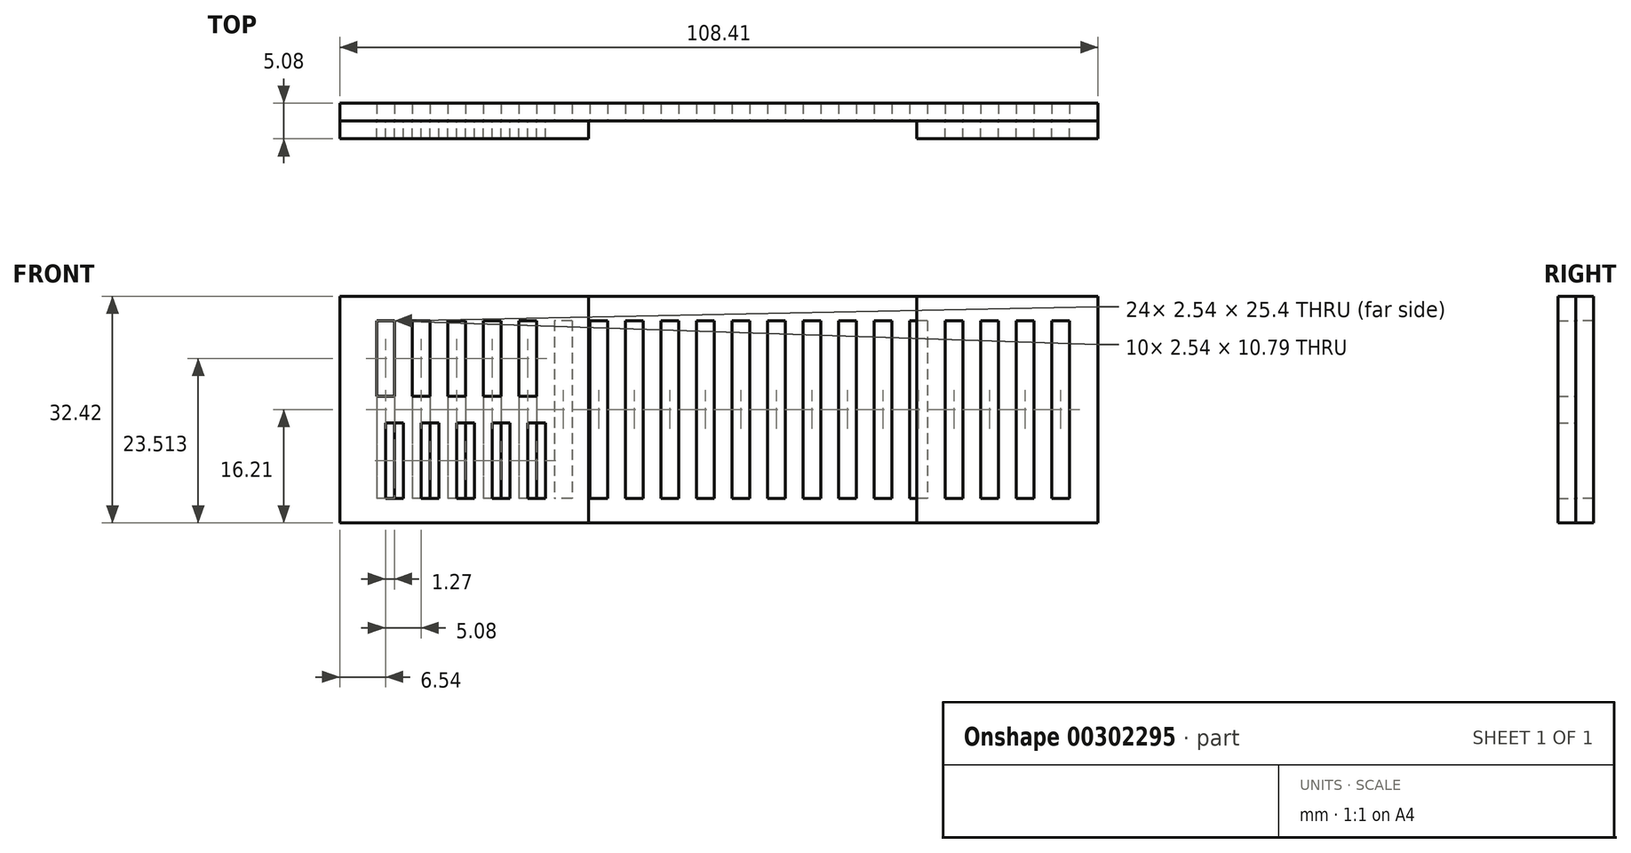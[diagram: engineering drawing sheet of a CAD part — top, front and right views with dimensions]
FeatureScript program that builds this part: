
annotation { "Feature Type Name" : "Feature", "Feature Type Description" : "" }
export const myFeature = defineFeature(function(context is Context, id is Id, definition is map)
    precondition{}
    {
        {
            var Q0;
            Q0=qCreatedBy(makeId("Front.planeOp"),FACE);
            var sketch = newSketch(context, id + "F0", { "sketchPlane" : qUnion([Q0])});
            skLineSegment(sketch, "E0.bottom", {"start": v(1.27, 12.7) * mm, "end": v(-1.27, 12.7) * mm});
            skLineSegment(sketch, "E0.top", {"start": v(1.27, -12.7) * mm, "end": v(-1.27, -12.7) * mm});
            skLineSegment(sketch, "E0.left", {"start": v(1.27, 12.7) * mm, "end": v(1.27, -12.7) * mm});
            skLineSegment(sketch, "E0.right", {"start": v(-1.27, 12.7) * mm, "end": v(-1.27, -12.7) * mm});
            skPoint(sketch, "E0.middle", {"position": v(0, 0) * mm});
            skLineSegment(sketch, "E1.1.0.0", {"start": v(6.35, 12.7) * mm, "end": v(6.35, -12.7) * mm});
            skLineSegment(sketch, "E1.1.0.1", {"start": v(3.81, 12.7) * mm, "end": v(3.81, -12.7) * mm});
            skPoint(sketch, "E1.1.0.2", {"position": v(5.08, 0) * mm});
            skLineSegment(sketch, "E1.1.0.3", {"start": v(6.35, 12.7) * mm, "end": v(3.81, 12.7) * mm});
            skLineSegment(sketch, "E1.1.0.4", {"start": v(6.35, -12.7) * mm, "end": v(3.81, -12.7) * mm});
            skLineSegment(sketch, "E1.2.0.0", {"start": v(11.43, 12.7) * mm, "end": v(11.43, -12.7) * mm});
            skLineSegment(sketch, "E1.2.0.1", {"start": v(8.9, 12.7) * mm, "end": v(8.9, -12.7) * mm});
            skPoint(sketch, "E1.2.0.2", {"position": v(10.16, 0) * mm});
            skLineSegment(sketch, "E1.2.0.3", {"start": v(11.43, 12.7) * mm, "end": v(8.9, 12.7) * mm});
            skLineSegment(sketch, "E1.2.0.4", {"start": v(11.43, -12.7) * mm, "end": v(8.9, -12.7) * mm});
            skLineSegment(sketch, "E1.3.0.0", {"start": v(16.51, 12.7) * mm, "end": v(16.51, -12.7) * mm});
            skLineSegment(sketch, "E1.3.0.1", {"start": v(13.97, 12.7) * mm, "end": v(13.97, -12.7) * mm});
            skPoint(sketch, "E1.3.0.2", {"position": v(15.24, 0) * mm});
            skLineSegment(sketch, "E1.3.0.3", {"start": v(16.51, 12.7) * mm, "end": v(13.97, 12.7) * mm});
            skLineSegment(sketch, "E1.3.0.4", {"start": v(16.51, -12.7) * mm, "end": v(13.97, -12.7) * mm});
            skLineSegment(sketch, "E1.4.0.0", {"start": v(21.6, 12.7) * mm, "end": v(21.6, -12.7) * mm});
            skLineSegment(sketch, "E1.4.0.1", {"start": v(19.05, 12.7) * mm, "end": v(19.05, -12.7) * mm});
            skPoint(sketch, "E1.4.0.2", {"position": v(20.32, 0) * mm});
            skLineSegment(sketch, "E1.4.0.3", {"start": v(21.6, 12.7) * mm, "end": v(19.05, 12.7) * mm});
            skLineSegment(sketch, "E1.4.0.4", {"start": v(21.6, -12.7) * mm, "end": v(19.05, -12.7) * mm});
            skLineSegment(sketch, "E1.5.0.0", {"start": v(26.67, 12.7) * mm, "end": v(26.67, -12.7) * mm});
            skLineSegment(sketch, "E1.5.0.1", {"start": v(24.13, 12.7) * mm, "end": v(24.13, -12.7) * mm});
            skPoint(sketch, "E1.5.0.2", {"position": v(25.4, 0) * mm});
            skLineSegment(sketch, "E1.5.0.3", {"start": v(26.67, 12.7) * mm, "end": v(24.13, 12.7) * mm});
            skLineSegment(sketch, "E1.5.0.4", {"start": v(26.67, -12.7) * mm, "end": v(24.13, -12.7) * mm});
            skLineSegment(sketch, "E1.6.0.0", {"start": v(31.75, 12.7) * mm, "end": v(31.75, -12.7) * mm});
            skLineSegment(sketch, "E1.6.0.1", {"start": v(29.21, 12.7) * mm, "end": v(29.21, -12.7) * mm});
            skPoint(sketch, "E1.6.0.2", {"position": v(30.48, 0) * mm});
            skLineSegment(sketch, "E1.6.0.3", {"start": v(31.75, 12.7) * mm, "end": v(29.21, 12.7) * mm});
            skLineSegment(sketch, "E1.6.0.4", {"start": v(31.75, -12.7) * mm, "end": v(29.21, -12.7) * mm});
            skLineSegment(sketch, "E1.7.0.0", {"start": v(36.83, 12.7) * mm, "end": v(36.83, -12.7) * mm});
            skLineSegment(sketch, "E1.7.0.1", {"start": v(34.3, 12.7) * mm, "end": v(34.3, -12.7) * mm});
            skPoint(sketch, "E1.7.0.2", {"position": v(35.56, 0) * mm});
            skLineSegment(sketch, "E1.7.0.3", {"start": v(36.83, 12.7) * mm, "end": v(34.3, 12.7) * mm});
            skLineSegment(sketch, "E1.7.0.4", {"start": v(36.83, -12.7) * mm, "end": v(34.3, -12.7) * mm});
            skLineSegment(sketch, "E1.8.0.0", {"start": v(41.91, 12.7) * mm, "end": v(41.91, -12.7) * mm});
            skLineSegment(sketch, "E1.8.0.1", {"start": v(39.37, 12.7) * mm, "end": v(39.37, -12.7) * mm});
            skPoint(sketch, "E1.8.0.2", {"position": v(40.64, 0) * mm});
            skLineSegment(sketch, "E1.8.0.3", {"start": v(41.91, 12.7) * mm, "end": v(39.37, 12.7) * mm});
            skLineSegment(sketch, "E1.8.0.4", {"start": v(41.91, -12.7) * mm, "end": v(39.37, -12.7) * mm});
            skLineSegment(sketch, "E1.9.0.0", {"start": v(47, 12.7) * mm, "end": v(47, -12.7) * mm});
            skLineSegment(sketch, "E1.9.0.1", {"start": v(44.45, 12.7) * mm, "end": v(44.45, -12.7) * mm});
            skPoint(sketch, "E1.9.0.2", {"position": v(45.72, 0) * mm});
            skLineSegment(sketch, "E1.9.0.3", {"start": v(47, 12.7) * mm, "end": v(44.45, 12.7) * mm});
            skLineSegment(sketch, "E1.9.0.4", {"start": v(47, -12.7) * mm, "end": v(44.45, -12.7) * mm});
            skLineSegment(sketch, "E1.10.0.0", {"start": v(52.07, 12.7) * mm, "end": v(52.07, -12.7) * mm});
            skLineSegment(sketch, "E1.10.0.1", {"start": v(49.53, 12.7) * mm, "end": v(49.53, -12.7) * mm});
            skPoint(sketch, "E1.10.0.2", {"position": v(50.8, 0) * mm});
            skLineSegment(sketch, "E1.10.0.3", {"start": v(52.07, 12.7) * mm, "end": v(49.53, 12.7) * mm});
            skLineSegment(sketch, "E1.10.0.4", {"start": v(52.07, -12.7) * mm, "end": v(49.53, -12.7) * mm});
            skLineSegment(sketch, "E1.11.0.0", {"start": v(57.15, 12.7) * mm, "end": v(57.15, -12.7) * mm});
            skLineSegment(sketch, "E1.11.0.1", {"start": v(54.61, 12.7) * mm, "end": v(54.61, -12.7) * mm});
            skPoint(sketch, "E1.11.0.2", {"position": v(55.88, 0) * mm});
            skLineSegment(sketch, "E1.11.0.3", {"start": v(57.15, 12.7) * mm, "end": v(54.61, 12.7) * mm});
            skLineSegment(sketch, "E1.11.0.4", {"start": v(57.15, -12.7) * mm, "end": v(54.61, -12.7) * mm});
            skLineSegment(sketch, "E1.12.0.0", {"start": v(62.23, 12.7) * mm, "end": v(62.23, -12.7) * mm});
            skLineSegment(sketch, "E1.12.0.1", {"start": v(59.7, 12.7) * mm, "end": v(59.7, -12.7) * mm});
            skPoint(sketch, "E1.12.0.2", {"position": v(60.96, 0) * mm});
            skLineSegment(sketch, "E1.12.0.3", {"start": v(62.23, 12.7) * mm, "end": v(59.7, 12.7) * mm});
            skLineSegment(sketch, "E1.12.0.4", {"start": v(62.23, -12.7) * mm, "end": v(59.7, -12.7) * mm});
            skLineSegment(sketch, "E1.13.0.0", {"start": v(67.31, 12.7) * mm, "end": v(67.31, -12.7) * mm});
            skLineSegment(sketch, "E1.13.0.1", {"start": v(64.77, 12.7) * mm, "end": v(64.77, -12.7) * mm});
            skPoint(sketch, "E1.13.0.2", {"position": v(66.04, 0) * mm});
            skLineSegment(sketch, "E1.13.0.3", {"start": v(67.31, 12.7) * mm, "end": v(64.77, 12.7) * mm});
            skLineSegment(sketch, "E1.13.0.4", {"start": v(67.31, -12.7) * mm, "end": v(64.77, -12.7) * mm});
            skLineSegment(sketch, "E1.14.0.0", {"start": v(72.4, 12.7) * mm, "end": v(72.4, -12.7) * mm});
            skLineSegment(sketch, "E1.14.0.1", {"start": v(69.85, 12.7) * mm, "end": v(69.85, -12.7) * mm});
            skPoint(sketch, "E1.14.0.2", {"position": v(71.12, 0) * mm});
            skLineSegment(sketch, "E1.14.0.3", {"start": v(72.4, 12.7) * mm, "end": v(69.85, 12.7) * mm});
            skLineSegment(sketch, "E1.14.0.4", {"start": v(72.4, -12.7) * mm, "end": v(69.85, -12.7) * mm});
            skLineSegment(sketch, "E1.15.0.0", {"start": v(77.47, 12.7) * mm, "end": v(77.47, -12.7) * mm});
            skLineSegment(sketch, "E1.15.0.1", {"start": v(74.93, 12.7) * mm, "end": v(74.93, -12.7) * mm});
            skPoint(sketch, "E1.15.0.2", {"position": v(76.2, 0) * mm});
            skLineSegment(sketch, "E1.15.0.3", {"start": v(77.47, 12.7) * mm, "end": v(74.93, 12.7) * mm});
            skLineSegment(sketch, "E1.15.0.4", {"start": v(77.47, -12.7) * mm, "end": v(74.93, -12.7) * mm});
            skLineSegment(sketch, "E1.16.0.0", {"start": v(82.55, 12.7) * mm, "end": v(82.55, -12.7) * mm});
            skLineSegment(sketch, "E1.16.0.1", {"start": v(80.01, 12.7) * mm, "end": v(80.01, -12.7) * mm});
            skPoint(sketch, "E1.16.0.2", {"position": v(81.28, 0) * mm});
            skLineSegment(sketch, "E1.16.0.3", {"start": v(82.55, 12.7) * mm, "end": v(80.01, 12.7) * mm});
            skLineSegment(sketch, "E1.16.0.4", {"start": v(82.55, -12.7) * mm, "end": v(80.01, -12.7) * mm});
            skLineSegment(sketch, "E1.17.0.0", {"start": v(87.63, 12.7) * mm, "end": v(87.63, -12.7) * mm});
            skLineSegment(sketch, "E1.17.0.1", {"start": v(85.1, 12.7) * mm, "end": v(85.1, -12.7) * mm});
            skPoint(sketch, "E1.17.0.2", {"position": v(86.36, 0) * mm});
            skLineSegment(sketch, "E1.17.0.3", {"start": v(87.63, 12.7) * mm, "end": v(85.1, 12.7) * mm});
            skLineSegment(sketch, "E1.17.0.4", {"start": v(87.63, -12.7) * mm, "end": v(85.1, -12.7) * mm});
            skLineSegment(sketch, "E1.18.0.0", {"start": v(92.71, 12.7) * mm, "end": v(92.71, -12.7) * mm});
            skLineSegment(sketch, "E1.18.0.1", {"start": v(90.17, 12.7) * mm, "end": v(90.17, -12.7) * mm});
            skPoint(sketch, "E1.18.0.2", {"position": v(91.44, 0) * mm});
            skLineSegment(sketch, "E1.18.0.3", {"start": v(92.71, 12.7) * mm, "end": v(90.17, 12.7) * mm});
            skLineSegment(sketch, "E1.18.0.4", {"start": v(92.71, -12.7) * mm, "end": v(90.17, -12.7) * mm});
            skLineSegment(sketch, "E1.19.0.0", {"start": v(97.8, 12.7) * mm, "end": v(97.8, -12.7) * mm});
            skLineSegment(sketch, "E1.19.0.1", {"start": v(95.25, 12.7) * mm, "end": v(95.25, -12.7) * mm});
            skPoint(sketch, "E1.19.0.2", {"position": v(96.52, 0) * mm});
            skLineSegment(sketch, "E1.19.0.3", {"start": v(97.8, 12.7) * mm, "end": v(95.25, 12.7) * mm});
            skLineSegment(sketch, "E1.19.0.4", {"start": v(97.8, -12.7) * mm, "end": v(95.25, -12.7) * mm});
            skLineSegment(sketch, "E1.direction1", {"start": v(-1.27, -12.7) * mm, "end": v(3.81, -12.7) * mm, "construction": true});
            skLineSegment(sketch, "E2.bottom", {"start": v(-6.54, -16.21) * mm, "end": v(101.87, -16.21) * mm});
            skLineSegment(sketch, "E2.top", {"start": v(-6.54, 16.21) * mm, "end": v(101.87, 16.21) * mm});
            skLineSegment(sketch, "E2.left", {"start": v(-6.54, -16.21) * mm, "end": v(-6.54, 16.21) * mm});
            skLineSegment(sketch, "E2.right", {"start": v(101.87, -16.21) * mm, "end": v(101.87, 16.21) * mm});
            skLineSegment(sketch, "E3", {"start": v(75.95, 16.21) * mm, "end": v(75.95, -16.21) * mm});
            skSolve(sketch);
        }
        {
            var Q0;
            Q0=makeQuery(id+"F0.imprint","IMPRINT",FACE,{"disambiguationData":[TD([[makeQuery(id+"F0.imprint","IMPRINT",EDGE,{"derivedFrom":sQuery(id+"F0.wireOp",EDGE,"E0.bottom")}),-1.0]])]});
            var Q1;
            {var subQ2=sQuery(id+"F0.wireOp",EDGE,"E1.15.0.0");Q1=makeQuery(id+"F0.imprint","IMPRINT",FACE,{"disambiguationData":[TD([[makeQuery(id+"F0.imprint","IMPRINT",EDGE,{"derivedFrom":subQ2}),1.0]])]});}
            extrude(context, id + "F1", {"entities" : qUnion([Q0, Q1]), "oppositeDirection" : true, "depth" : 2.54 * mm});
        }
        {
            var Q0;
            {var subQ2=sQuery(id+"F0.wireOp",EDGE,"E1.15.0.0");Q0=makeQuery(id+"F0.imprint","IMPRINT",FACE,{"disambiguationData":[TD([[makeQuery(id+"F0.imprint","IMPRINT",EDGE,{"derivedFrom":subQ2}),1.0]])]});}
            var Q1;
            {var subQ0=sQuery(id+"F0.wireOp",EDGE,"E1.15.0.0");Q1=makeQuery(id+"F0.imprint","IMPRINT",FACE,{"disambiguationData":[TD([[makeQuery(id+"F0.imprint","IMPRINT",EDGE,{"derivedFrom":subQ0}),-1.0]])]});}
            extrude(context, id + "F2", {"entities" : qUnion([Q0, Q1]), "depth" : 2.54 * mm});
        }
        {
            var Q0;
            Q0=qCreatedBy(makeId("Front.planeOp"),FACE);
            var sketch = newSketch(context, id + "F3", { "sketchPlane" : qUnion([Q0])});
            skLineSegment(sketch, "E4.0", {"start": v(-6.54, -16.21) * mm, "end": v(-6.54, 16.21) * mm});
            skLineSegment(sketch, "E5.bottom", {"start": v(-6.54, -16.21) * mm, "end": v(29.02, -16.21) * mm});
            skLineSegment(sketch, "E5.top", {"start": v(-6.54, 16.21) * mm, "end": v(29.02, 16.21) * mm});
            skLineSegment(sketch, "E5.right", {"start": v(29.02, -16.21) * mm, "end": v(29.02, 16.21) * mm});
            skPoint(sketch, "E6.0", {"position": v(-1.27, 12.7) * mm});
            skPoint(sketch, "E7.0", {"position": v(1.27, 12.7) * mm});
            skLineSegment(sketch, "E8.bottom", {"start": v(-1.27, 12.7) * mm, "end": v(1.27, 12.7) * mm});
            skLineSegment(sketch, "E8.top", {"start": v(-1.27, 1.9) * mm, "end": v(1.27, 1.9) * mm});
            skLineSegment(sketch, "E8.left", {"start": v(-1.27, 12.7) * mm, "end": v(-1.27, 1.9) * mm});
            skLineSegment(sketch, "E8.right", {"start": v(1.27, 12.7) * mm, "end": v(1.27, 1.9) * mm});
            skPoint(sketch, "E9.0", {"position": v(0, -1.9) * mm});
            skPoint(sketch, "E10.0", {"position": v(2.54, -1.82) * mm});
            skLineSegment(sketch, "E11.bottom", {"start": v(0, -1.9) * mm, "end": v(2.54, -1.9) * mm});
            skLineSegment(sketch, "E11.top", {"start": v(0, -12.7) * mm, "end": v(2.54, -12.7) * mm});
            skLineSegment(sketch, "E11.left", {"start": v(0, -1.9) * mm, "end": v(0, -12.7) * mm});
            skLineSegment(sketch, "E11.right", {"start": v(2.54, -1.9) * mm, "end": v(2.54, -12.7) * mm});
            skPoint(sketch, "E12.0", {"position": v(-1.27, -12.7) * mm});
            skPoint(sketch, "E13.1.0.0", {"position": v(3.81, -12.7) * mm});
            skPoint(sketch, "E13.1.0.1", {"position": v(5.08, -1.9) * mm});
            skLineSegment(sketch, "E13.1.0.2", {"start": v(3.81, 1.9) * mm, "end": v(6.35, 1.9) * mm});
            skPoint(sketch, "E13.1.0.3", {"position": v(3.81, 12.7) * mm});
            skLineSegment(sketch, "E13.1.0.4", {"start": v(3.81, 12.7) * mm, "end": v(3.81, 1.9) * mm});
            skLineSegment(sketch, "E13.1.0.5", {"start": v(6.35, 12.7) * mm, "end": v(6.35, 1.9) * mm});
            skPoint(sketch, "E13.1.0.6", {"position": v(6.35, 12.7) * mm});
            skLineSegment(sketch, "E13.1.0.7", {"start": v(3.81, 12.7) * mm, "end": v(6.35, 12.7) * mm});
            skPoint(sketch, "E13.1.0.8", {"position": v(7.62, -1.82) * mm});
            skLineSegment(sketch, "E13.1.0.9", {"start": v(5.08, -1.9) * mm, "end": v(5.08, -12.7) * mm});
            skLineSegment(sketch, "E13.1.0.10", {"start": v(7.62, -1.9) * mm, "end": v(7.62, -12.7) * mm});
            skLineSegment(sketch, "E13.1.0.11", {"start": v(5.08, -1.9) * mm, "end": v(7.62, -1.9) * mm});
            skLineSegment(sketch, "E13.1.0.12", {"start": v(5.08, -12.7) * mm, "end": v(7.62, -12.7) * mm});
            skPoint(sketch, "E13.2.0.0", {"position": v(8.9, -12.7) * mm});
            skPoint(sketch, "E13.2.0.1", {"position": v(10.16, -1.9) * mm});
            skLineSegment(sketch, "E13.2.0.2", {"start": v(8.9, 1.9) * mm, "end": v(11.43, 1.9) * mm});
            skPoint(sketch, "E13.2.0.3", {"position": v(8.9, 12.7) * mm});
            skLineSegment(sketch, "E13.2.0.4", {"start": v(8.9, 12.7) * mm, "end": v(8.9, 1.9) * mm});
            skLineSegment(sketch, "E13.2.0.5", {"start": v(11.43, 12.7) * mm, "end": v(11.43, 1.9) * mm});
            skPoint(sketch, "E13.2.0.6", {"position": v(11.43, 12.7) * mm});
            skLineSegment(sketch, "E13.2.0.7", {"start": v(8.9, 12.7) * mm, "end": v(11.43, 12.7) * mm});
            skPoint(sketch, "E13.2.0.8", {"position": v(12.7, -1.82) * mm});
            skLineSegment(sketch, "E13.2.0.9", {"start": v(10.16, -1.9) * mm, "end": v(10.16, -12.7) * mm});
            skLineSegment(sketch, "E13.2.0.10", {"start": v(12.7, -1.9) * mm, "end": v(12.7, -12.7) * mm});
            skLineSegment(sketch, "E13.2.0.11", {"start": v(10.16, -1.9) * mm, "end": v(12.7, -1.9) * mm});
            skLineSegment(sketch, "E13.2.0.12", {"start": v(10.16, -12.7) * mm, "end": v(12.7, -12.7) * mm});
            skPoint(sketch, "E13.3.0.0", {"position": v(13.97, -12.7) * mm});
            skPoint(sketch, "E13.3.0.1", {"position": v(15.24, -1.9) * mm});
            skLineSegment(sketch, "E13.3.0.2", {"start": v(13.97, 1.9) * mm, "end": v(16.51, 1.9) * mm});
            skPoint(sketch, "E13.3.0.3", {"position": v(13.97, 12.7) * mm});
            skLineSegment(sketch, "E13.3.0.4", {"start": v(13.97, 12.7) * mm, "end": v(13.97, 1.9) * mm});
            skLineSegment(sketch, "E13.3.0.5", {"start": v(16.51, 12.7) * mm, "end": v(16.51, 1.9) * mm});
            skPoint(sketch, "E13.3.0.6", {"position": v(16.51, 12.7) * mm});
            skLineSegment(sketch, "E13.3.0.7", {"start": v(13.97, 12.7) * mm, "end": v(16.51, 12.7) * mm});
            skPoint(sketch, "E13.3.0.8", {"position": v(17.78, -1.82) * mm});
            skLineSegment(sketch, "E13.3.0.9", {"start": v(15.24, -1.9) * mm, "end": v(15.24, -12.7) * mm});
            skLineSegment(sketch, "E13.3.0.10", {"start": v(17.78, -1.9) * mm, "end": v(17.78, -12.7) * mm});
            skLineSegment(sketch, "E13.3.0.11", {"start": v(15.24, -1.9) * mm, "end": v(17.78, -1.9) * mm});
            skLineSegment(sketch, "E13.3.0.12", {"start": v(15.24, -12.7) * mm, "end": v(17.78, -12.7) * mm});
            skPoint(sketch, "E13.4.0.0", {"position": v(19.05, -12.7) * mm});
            skPoint(sketch, "E13.4.0.1", {"position": v(20.32, -1.9) * mm});
            skLineSegment(sketch, "E13.4.0.2", {"start": v(19.05, 1.9) * mm, "end": v(21.6, 1.9) * mm});
            skPoint(sketch, "E13.4.0.3", {"position": v(19.05, 12.7) * mm});
            skLineSegment(sketch, "E13.4.0.4", {"start": v(19.05, 12.7) * mm, "end": v(19.05, 1.9) * mm});
            skLineSegment(sketch, "E13.4.0.5", {"start": v(21.6, 12.7) * mm, "end": v(21.6, 1.9) * mm});
            skPoint(sketch, "E13.4.0.6", {"position": v(21.6, 12.7) * mm});
            skLineSegment(sketch, "E13.4.0.7", {"start": v(19.05, 12.7) * mm, "end": v(21.6, 12.7) * mm});
            skPoint(sketch, "E13.4.0.8", {"position": v(22.86, -1.82) * mm});
            skLineSegment(sketch, "E13.4.0.9", {"start": v(20.32, -1.9) * mm, "end": v(20.32, -12.7) * mm});
            skLineSegment(sketch, "E13.4.0.10", {"start": v(22.86, -1.9) * mm, "end": v(22.86, -12.7) * mm});
            skLineSegment(sketch, "E13.4.0.11", {"start": v(20.32, -1.9) * mm, "end": v(22.86, -1.9) * mm});
            skLineSegment(sketch, "E13.4.0.12", {"start": v(20.32, -12.7) * mm, "end": v(22.86, -12.7) * mm});
            skLineSegment(sketch, "E13.direction1", {"start": v(-1.27, -12.7) * mm, "end": v(3.81, -12.7) * mm, "construction": true});
            skSolve(sketch);
        }
        {
            var Q0;
            Q0=makeQuery(id+"F3.imprint","IMPRINT",FACE,{"disambiguationData":[TD([[makeQuery(id+"F3.imprint","IMPRINT",EDGE,{"derivedFrom":sQuery(id+"F3.wireOp",EDGE,"E5.bottom")}),1.0]])]});
            extrude(context, id + "F4", {"entities" : qUnion([Q0]), "depth" : 2.54 * mm});
        }
    });
